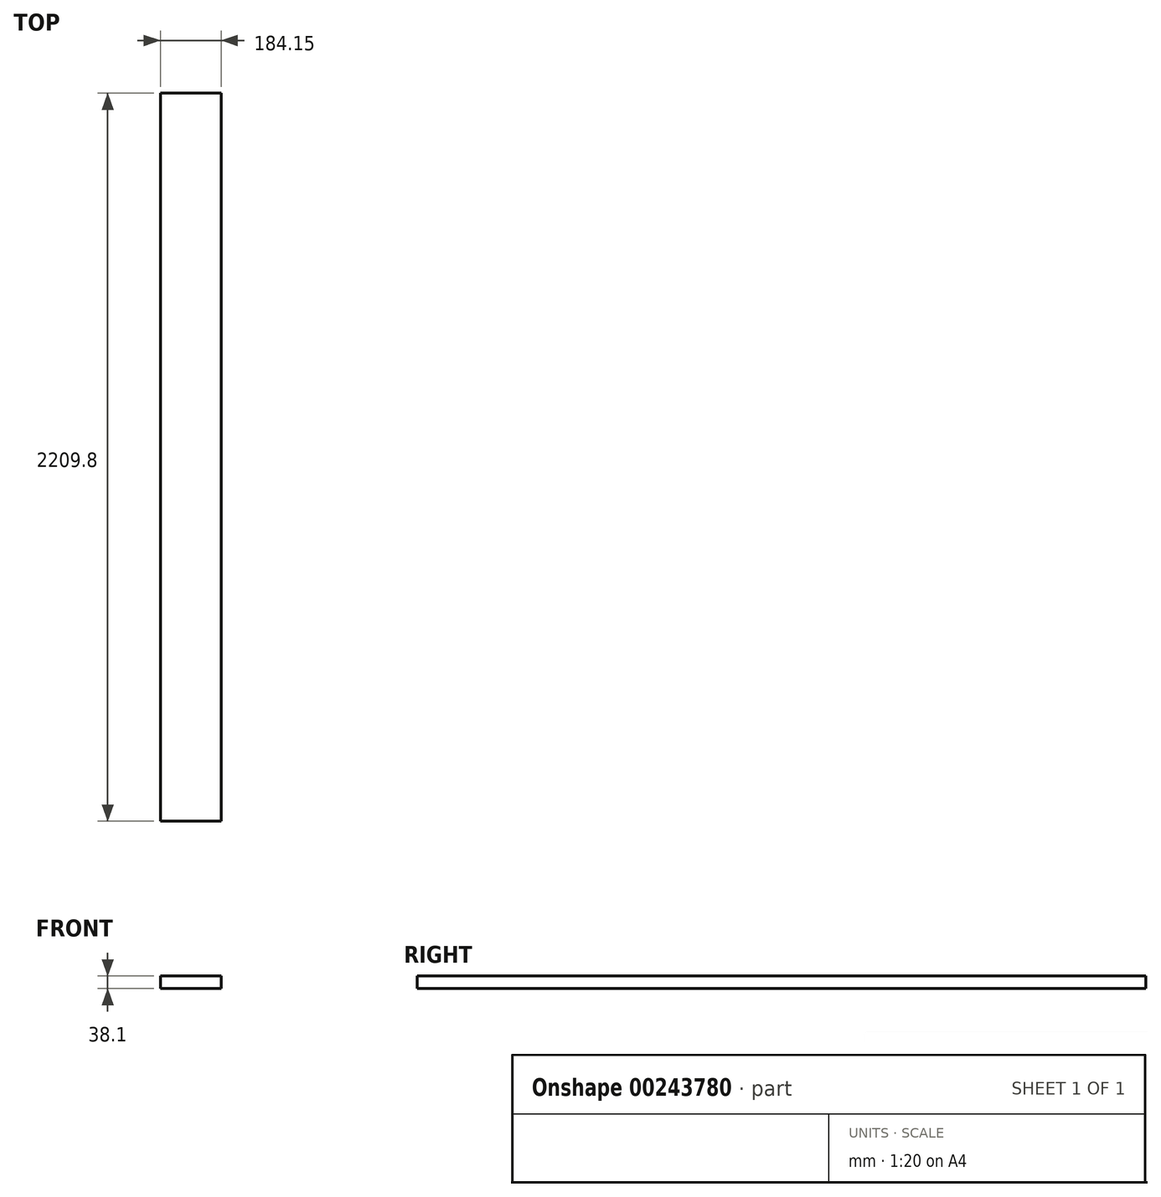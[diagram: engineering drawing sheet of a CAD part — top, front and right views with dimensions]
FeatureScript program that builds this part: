
annotation { "Feature Type Name" : "Feature", "Feature Type Description" : "" }
export const myFeature = defineFeature(function(context is Context, id is Id, definition is map)
    precondition{}
    {
        {
            var Q0;
            Q0=qCreatedBy(makeId("Front.planeOp"),FACE);
            var sketch = newSketch(context, id + "F0", { "sketchPlane" : qUnion([Q0])});
            skLineSegment(sketch, "E0.bottom", {"start": v(-107.62, 9.95) * mm, "end": v(76.53, 9.95) * mm});
            skLineSegment(sketch, "E0.top", {"start": v(-107.62, -28.15) * mm, "end": v(76.53, -28.15) * mm});
            skLineSegment(sketch, "E0.left", {"start": v(-107.62, 9.95) * mm, "end": v(-107.62, -28.15) * mm});
            skLineSegment(sketch, "E0.right", {"start": v(76.53, 9.95) * mm, "end": v(76.53, -28.15) * mm});
            skSolve(sketch);
        }
        {
            var Q0;
            Q0=makeQuery(id+"F0.imprint","IMPRINT",FACE,{"disambiguationData":[TD([[makeQuery(id+"F0.imprint","IMPRINT",EDGE,{"derivedFrom":sQuery(id+"F0.wireOp",EDGE,"E0.bottom")}),-1.0]])]});
            extrude(context, id + "F1", {"entities" : qUnion([Q0]), "depth" : 2209.8 * mm});
        }
    });
